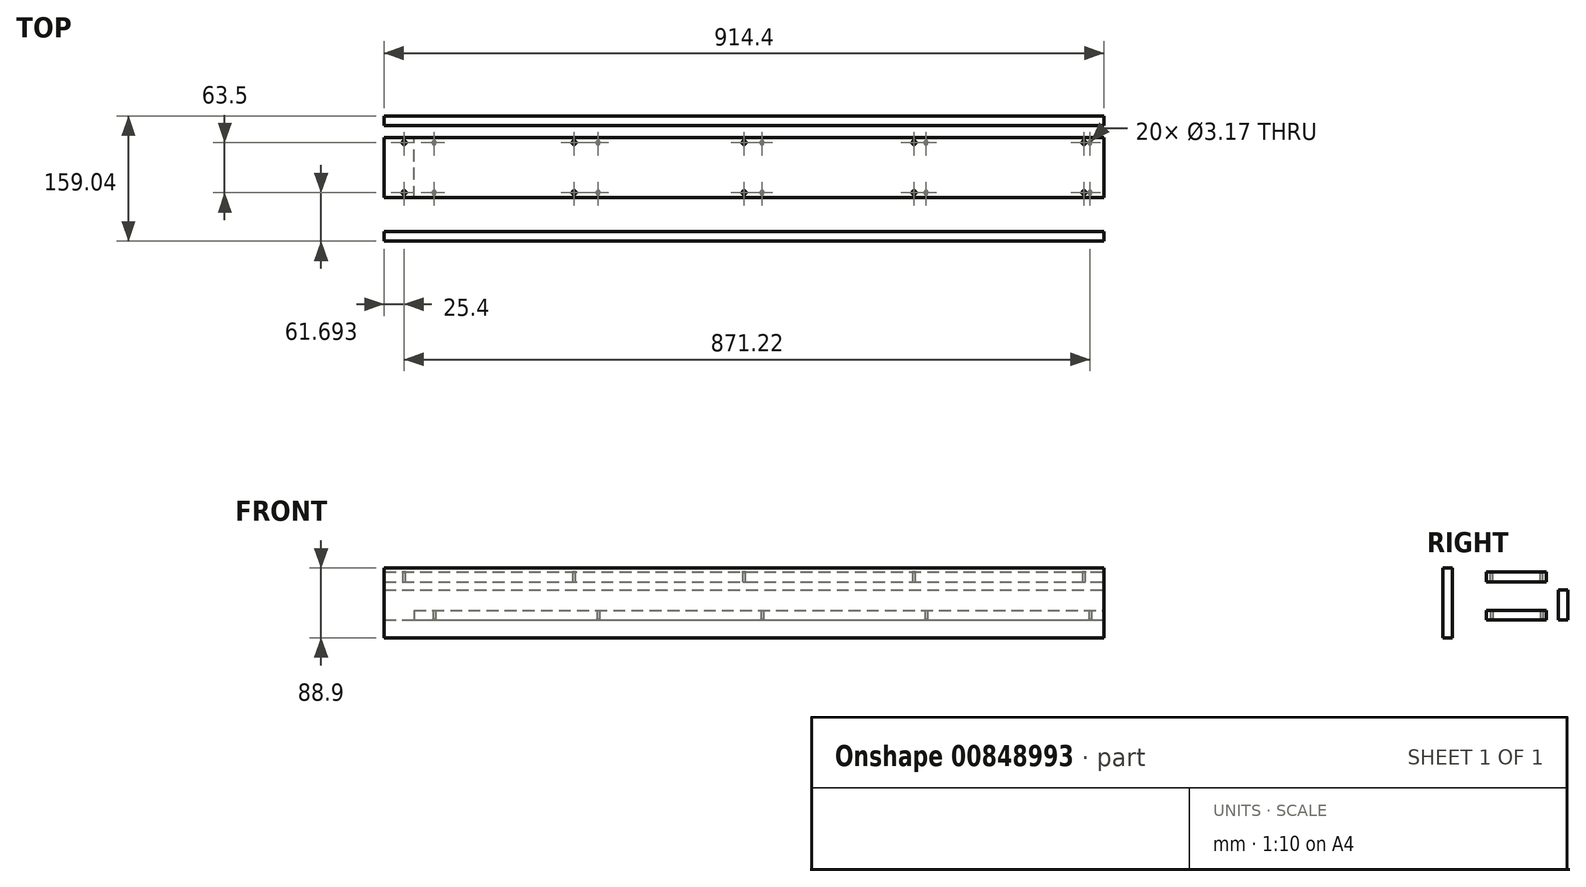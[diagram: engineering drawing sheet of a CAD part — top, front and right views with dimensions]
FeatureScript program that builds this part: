
annotation { "Feature Type Name" : "Feature", "Feature Type Description" : "" }
export const myFeature = defineFeature(function(context is Context, id is Id, definition is map)
    precondition{}
    {
        {
            var Q0;
            Q0=qCreatedBy(makeId("Right.planeOp"),FACE);
            var sketch = newSketch(context, id + "F0", { "sketchPlane" : qUnion([Q0])});
            skLineSegment(sketch, "E0.bottom", {"start": v(-27.99, 16.1) * mm, "end": v(48.21, 16.1) * mm});
            skLineSegment(sketch, "E0.top", {"start": v(-27.99, 3.8) * mm, "end": v(48.21, 3.8) * mm});
            skLineSegment(sketch, "E0.left", {"start": v(-27.99, 16.1) * mm, "end": v(-27.99, 3.8) * mm});
            skLineSegment(sketch, "E0.right", {"start": v(48.21, 16.1) * mm, "end": v(48.21, 3.8) * mm});
            skLineSegment(sketch, "E1.bottom", {"start": v(63.42, 4.15) * mm, "end": v(75.71, 4.15) * mm});
            skLineSegment(sketch, "E1.top", {"start": v(63.42, 42.25) * mm, "end": v(75.71, 42.25) * mm});
            skLineSegment(sketch, "E1.left", {"start": v(63.42, 4.15) * mm, "end": v(63.42, 42.25) * mm});
            skLineSegment(sketch, "E1.right", {"start": v(75.71, 4.15) * mm, "end": v(75.71, 42.25) * mm});
            skLineSegment(sketch, "E2.bottom", {"start": v(-27.99, 52.35) * mm, "end": v(48.21, 52.35) * mm});
            skLineSegment(sketch, "E2.top", {"start": v(-27.99, 64.64) * mm, "end": v(48.21, 64.64) * mm});
            skLineSegment(sketch, "E2.left", {"start": v(-27.99, 52.35) * mm, "end": v(-27.99, 64.64) * mm});
            skLineSegment(sketch, "E2.right", {"start": v(48.21, 52.35) * mm, "end": v(48.21, 64.64) * mm});
            skLineSegment(sketch, "E3.bottom", {"start": v(-83.33, 70) * mm, "end": v(-71.04, 70) * mm});
            skLineSegment(sketch, "E3.top", {"start": v(-83.33, -18.9) * mm, "end": v(-71.04, -18.9) * mm});
            skLineSegment(sketch, "E3.left", {"start": v(-83.33, 70) * mm, "end": v(-83.33, -18.9) * mm});
            skLineSegment(sketch, "E3.right", {"start": v(-71.04, 70) * mm, "end": v(-71.04, -18.9) * mm});
            skSolve(sketch);
        }
        {
            var Q0;
            Q0=makeQuery(id+"F0.imprint","IMPRINT",FACE,{"disambiguationData":[TD([[makeQuery(id+"F0.imprint","IMPRINT",EDGE,{"derivedFrom":sQuery(id+"F0.wireOp",EDGE,"E0.bottom")}),-1.0]])]});
            extrude(context, id + "F1", {"entities" : qUnion([Q0]), "oppositeDirection" : true, "depth" : 876.3 * mm, "offsetDistance" : 25.4 * mm});
        }
        {
            var Q0;
            Q0=makeQuery(id+"F0.imprint","IMPRINT",FACE,{"disambiguationData":[TD([[makeQuery(id+"F0.imprint","IMPRINT",EDGE,{"derivedFrom":sQuery(id+"F0.wireOp",EDGE,"E2.bottom")}),1.0]])]});
            var Q1;
            Q1=makeQuery(id+"F0.imprint","IMPRINT",FACE,{"disambiguationData":[TD([[makeQuery(id+"F0.imprint","IMPRINT",EDGE,{"derivedFrom":sQuery(id+"F0.wireOp",EDGE,"E1.bottom")}),1.0]])]});
            var Q2;
            Q2=makeQuery(id+"F0.imprint","IMPRINT",FACE,{"disambiguationData":[TD([[makeQuery(id+"F0.imprint","IMPRINT",EDGE,{"derivedFrom":sQuery(id+"F0.wireOp",EDGE,"E3.bottom")}),-1.0]])]});
            extrude(context, id + "F2", {"entities" : qUnion([Q0, Q1, Q2]), "oppositeDirection" : true, "depth" : 914.4 * mm, "offsetDistance" : 25.4 * mm});
        }
        {
            var Q0;
            Q0=makeQuery(id+"F1.opExtrude","SWEPT_FACE",FACE,{"disambiguationData":[OSD([sQuery(id+"F0.wireOp",EDGE,"E0.top")])]});
            var sketch = newSketch(context, id + "F3", { "sketchPlane" : qUnion([Q0])});
            skPoint(sketch, "E4", {"position": v(-850.9, 21.64) * mm});
            skPoint(sketch, "E5.0.1.0", {"position": v(-850.9, -41.86) * mm});
            skPoint(sketch, "E5.1.0.0", {"position": v(-642.62, 21.64) * mm});
            skPoint(sketch, "E5.1.1.0", {"position": v(-642.62, -41.86) * mm});
            skPoint(sketch, "E5.2.0.0", {"position": v(-434.34, 21.64) * mm});
            skPoint(sketch, "E5.2.1.0", {"position": v(-434.34, -41.86) * mm});
            skPoint(sketch, "E5.3.0.0", {"position": v(-226.06, 21.64) * mm});
            skPoint(sketch, "E5.3.1.0", {"position": v(-226.06, -41.86) * mm});
            skPoint(sketch, "E5.4.0.0", {"position": v(-17.78, 21.64) * mm});
            skPoint(sketch, "E5.4.1.0", {"position": v(-17.78, -41.86) * mm});
            skLineSegment(sketch, "E5.direction1", {"start": v(-850.9, 21.64) * mm, "end": v(-642.62, 21.64) * mm, "construction": true});
            skLineSegment(sketch, "E5.direction2", {"start": v(-850.9, 21.64) * mm, "end": v(-850.9, -41.86) * mm, "construction": true});
            skSolve(sketch);
        }
        {
            var Q0;
            Q0=sQuery(id+"F3.wireOp",VERTEX,"E4");
            var Q1;
            Q1=sQuery(id+"F3.wireOp",VERTEX,"E5.0.1.0");
            var Q2;
            Q2=sQuery(id+"F3.wireOp",VERTEX,"E5.1.1.0");
            var Q3;
            Q3=sQuery(id+"F3.wireOp",VERTEX,"E5.1.0.0");
            var Q4;
            Q4=sQuery(id+"F3.wireOp",VERTEX,"E5.2.1.0");
            var Q5;
            Q5=sQuery(id+"F3.wireOp",VERTEX,"E5.2.0.0");
            var Q6;
            Q6=sQuery(id+"F3.wireOp",VERTEX,"E5.3.0.0");
            var Q7;
            Q7=sQuery(id+"F3.wireOp",VERTEX,"E5.4.1.0");
            var Q8;
            Q8=sQuery(id+"F3.wireOp",VERTEX,"E5.4.0.0");
            var Q9;
            Q9=sQuery(id+"F3.wireOp",VERTEX,"E5.3.1.0");
            var Q10;
            Q10=makeQuery(id+"F1.opExtrude","SWEPT_BODY",BODY,{"disambiguationData":[OSD([sQuery(id+"F0.wireOp",EDGE,"E0.bottom"),sQuery(id+"F0.wireOp",EDGE,"E0.top"),sQuery(id+"F0.wireOp",EDGE,"E0.left"),sQuery(id+"F0.wireOp",EDGE,"E0.right")])]});
            hole(context, id + "F4", {"style" : HoleStyle.C_SINK, "endStyle" : HoleEndStyle.BLIND, "holeDiameter" : 3.17 * mm, "cSinkDiameter" : 5.08 * mm, "cSinkAngle" : 82 * degree, "majorDiameter" : 6.35 * mm, "holeDepth" : 12.7 * mm, "isTappedThrough" : true, "tappedDepth" : 12.7 * mm, "tapClearance" : 3, "startFromSketch" : true, "locations" : qUnion([Q0, Q1, Q2, Q3, Q4, Q5, Q6, Q7, Q8, Q9]), "scope" : qUnion([Q10])});
        }
        {
            var Q0;
            Q0=makeQuery(id+"F2.opExtrude","SWEPT_FACE",FACE,{"disambiguationData":[OSD([sQuery(id+"F0.wireOp",EDGE,"E2.top")])]});
            var sketch = newSketch(context, id + "F5", { "sketchPlane" : qUnion([Q0])});
            skPoint(sketch, "E6", {"position": v(-889, 41.86) * mm});
            skPoint(sketch, "E7.0.1.0", {"position": v(-889, -21.64) * mm});
            skPoint(sketch, "E7.1.0.0", {"position": v(-673.1, 41.86) * mm});
            skPoint(sketch, "E7.1.1.0", {"position": v(-673.1, -21.64) * mm});
            skPoint(sketch, "E7.2.0.0", {"position": v(-457.2, 41.86) * mm});
            skPoint(sketch, "E7.2.1.0", {"position": v(-457.2, -21.64) * mm});
            skPoint(sketch, "E7.3.0.0", {"position": v(-241.3, 41.86) * mm});
            skPoint(sketch, "E7.3.1.0", {"position": v(-241.3, -21.64) * mm});
            skPoint(sketch, "E7.4.0.0", {"position": v(-25.4, 41.86) * mm});
            skPoint(sketch, "E7.4.1.0", {"position": v(-25.4, -21.64) * mm});
            skLineSegment(sketch, "E7.direction1", {"start": v(-889, 41.86) * mm, "end": v(-673.1, 41.86) * mm, "construction": true});
            skLineSegment(sketch, "E7.direction2", {"start": v(-889, 41.86) * mm, "end": v(-889, -21.64) * mm, "construction": true});
            skSolve(sketch);
        }
        {
            var Q0;
            Q0=sQuery(id+"F5.wireOp",VERTEX,"E6");
            var Q1;
            Q1=sQuery(id+"F5.wireOp",VERTEX,"E7.0.1.0");
            var Q2;
            Q2=sQuery(id+"F5.wireOp",VERTEX,"E7.1.1.0");
            var Q3;
            Q3=sQuery(id+"F5.wireOp",VERTEX,"E7.1.0.0");
            var Q4;
            Q4=sQuery(id+"F5.wireOp",VERTEX,"E7.2.0.0");
            var Q5;
            Q5=sQuery(id+"F5.wireOp",VERTEX,"E7.2.1.0");
            var Q6;
            Q6=sQuery(id+"F5.wireOp",VERTEX,"E7.3.0.0");
            var Q7;
            Q7=sQuery(id+"F5.wireOp",VERTEX,"E7.3.1.0");
            var Q8;
            Q8=sQuery(id+"F5.wireOp",VERTEX,"E7.4.1.0");
            var Q9;
            Q9=sQuery(id+"F5.wireOp",VERTEX,"E7.4.0.0");
            var Q10;
            Q10=makeQuery(id+"F2.opExtrude","SWEPT_BODY",BODY,{"disambiguationData":[OSD([sQuery(id+"F0.wireOp",EDGE,"E2.bottom"),sQuery(id+"F0.wireOp",EDGE,"E2.top"),sQuery(id+"F0.wireOp",EDGE,"E2.left"),sQuery(id+"F0.wireOp",EDGE,"E2.right")])]});
            hole(context, id + "F6", {"style" : HoleStyle.C_SINK, "endStyle" : HoleEndStyle.BLIND, "holeDiameter" : 3.17 * mm, "cSinkDiameter" : 5.08 * mm, "cSinkAngle" : 82 * degree, "majorDiameter" : 6.35 * mm, "holeDepth" : 12.7 * mm, "isTappedThrough" : true, "tappedDepth" : 12.7 * mm, "tapClearance" : 3, "startFromSketch" : true, "locations" : qUnion([Q0, Q1, Q2, Q3, Q4, Q5, Q6, Q7, Q8, Q9]), "scope" : qUnion([Q10])});
        }
    });
